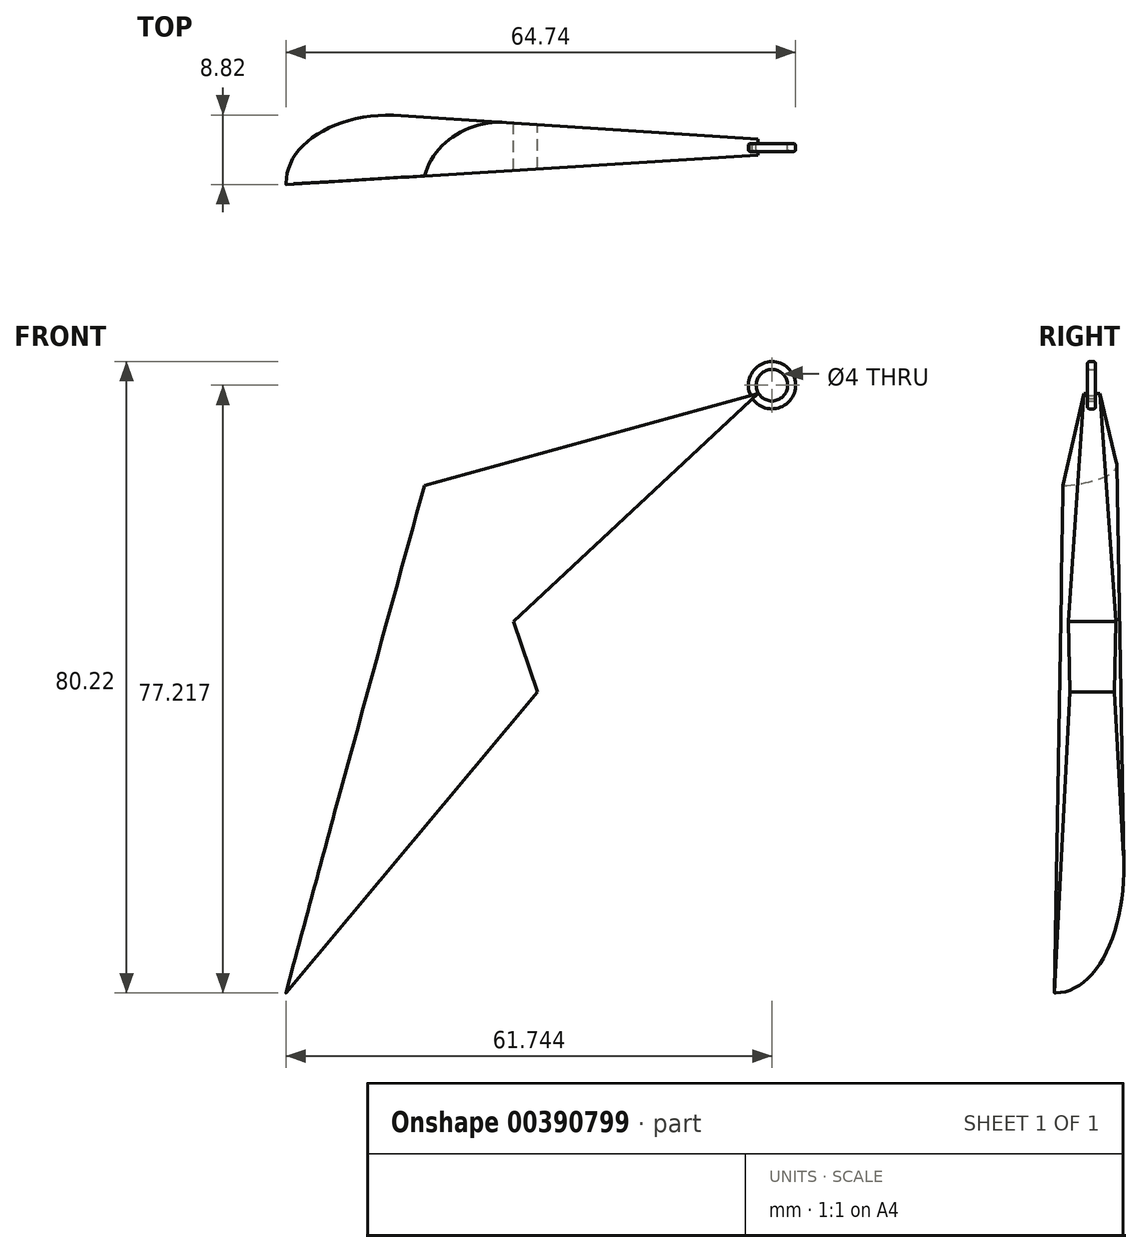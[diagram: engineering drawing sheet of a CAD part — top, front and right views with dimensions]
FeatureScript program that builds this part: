
annotation { "Feature Type Name" : "Feature", "Feature Type Description" : "" }
export const myFeature = defineFeature(function(context is Context, id is Id, definition is map)
    precondition{}
    {
        {
            var Q0;
            Q0=qCreatedBy(makeId("Front.planeOp"),FACE);
            var sketch = newSketch(context, id + "F0", { "sketchPlane" : qUnion([Q0])});
            skLineSegment(sketch, "E0", {"start": v(-11.57, 18.72) * mm, "end": v(-28.9, -45.65) * mm});
            skLineSegment(sketch, "E1", {"start": v(-28.9, -45.65) * mm, "end": v(3.1, -7.37) * mm});
            skLineSegment(sketch, "E2", {"start": v(3.1, -7.37) * mm, "end": v(0, 1.58) * mm});
            skLineSegment(sketch, "E3", {"start": v(0, 1.58) * mm, "end": v(31.1, 30.53) * mm});
            skLineSegment(sketch, "E4", {"start": v(31.1, 30.53) * mm, "end": v(-11.57, 18.72) * mm});
            skSolve(sketch);
        }
        {
            var Q0;
            Q0=makeQuery(id+"F0.imprint","IMPRINT",FACE,{"disambiguationData":[TD([[makeQuery(id+"F0.imprint","IMPRINT",EDGE,{"derivedFrom":sQuery(id+"F0.wireOp",EDGE,"E0")}),1.0]])]});
            extrude(context, id + "F1", {"entities" : qUnion([Q0]), "depth" : 5 * mm, "hasSecondDirection" : true, "secondDirectionOppositeDirection" : true, "secondDirectionDepth" : 5 * mm});
        }
        {
            var Q0;
            Q0=qCreatedBy(makeId("Top.planeOp"),FACE);
            var sketch = newSketch(context, id + "F2", { "sketchPlane" : qUnion([Q0])});
            skLineSegment(sketch, "E5", {"start": v(-39.09, 5.72) * mm, "end": v(-39.09, -5.33) * mm});
            skLineSegment(sketch, "E6", {"start": v(-39.09, -5.33) * mm, "end": v(47.13, 0) * mm});
            skLineSegment(sketch, "E7", {"start": v(47.13, 0) * mm, "end": v(-39.09, 5.72) * mm});
            skLineSegment(sketch, "E8", {"start": v(-48.28, 20.76) * mm, "end": v(52.08, 20.76) * mm});
            skLineSegment(sketch, "E9", {"start": v(52.08, 20.76) * mm, "end": v(52.08, -13.52) * mm});
            skLineSegment(sketch, "E10", {"start": v(52.08, -13.52) * mm, "end": v(-48.28, -13.52) * mm});
            skLineSegment(sketch, "E11", {"start": v(-48.28, -13.52) * mm, "end": v(-48.28, 20.76) * mm});
            skSolve(sketch);
        }
        {
            var Q0;
            Q0=makeQuery(id+"F2.imprint","IMPRINT",FACE,{"disambiguationData":[TD([[makeQuery(id+"F2.imprint","IMPRINT",EDGE,{"derivedFrom":sQuery(id+"F2.wireOp",EDGE,"E5")}),-1.0]])]});
            extrude(context, id + "F3", {"entities" : qUnion([Q0]), "operationType" : NewBodyOperationType.REMOVE, "oppositeDirection" : true, "depth" : 63.9 * mm, "hasSecondDirection" : true, "secondDirectionOppositeDirection" : false, "secondDirectionDepth" : 50 * mm});
        }
        {
            var Q0;
            Q0=makeQuery(id+"F3.boolean.opBoolean","INTERSECT",EDGE,{"derivedFrom":[makeQuery(id+"F1.opExtrude","SWEPT_FACE",FACE,{"disambiguationData":[OSD([sQuery(id+"F0.wireOp",EDGE,"E0")])]}),makeQuery(id+"F3.opExtrude","SWEPT_FACE",FACE,{"disambiguationData":[OSD([sQuery(id+"F2.wireOp",EDGE,"E6")])]})]});
            fillet(context, id + "F4", {"entities" : qUnion([Q0]), "radius" : 0.02 * mm, "tangentPropagation" : true, "allowEdgeOverflow" : false});
        }
        {
            var Q0;
            Q0=makeQuery(id+"F3.boolean.opBoolean","INTERSECT",EDGE,{"derivedFrom":[makeQuery(id+"F1.opExtrude","SWEPT_FACE",FACE,{"disambiguationData":[OSD([sQuery(id+"F0.wireOp",EDGE,"E0")])]}),makeQuery(id+"F3.opExtrude","SWEPT_FACE",FACE,{"disambiguationData":[OSD([sQuery(id+"F2.wireOp",EDGE,"E7")])]})]});
            var Q1;
            {var subQ0=makeQuery(id+"F1.opExtrude","SWEPT_FACE",FACE,{"disambiguationData":[OSD([sQuery(id+"F0.wireOp",EDGE,"E0")])]});Q1=makeQuery(id+"F4.opFillet","BLEND_EDGE",EDGE,{"blendedFrom":[makeQuery(id+"F3.boolean.opBoolean","INTERSECT",EDGE,{"derivedFrom":[subQ0,makeQuery(id+"F3.opExtrude","SWEPT_FACE",FACE,{"disambiguationData":[OSD([sQuery(id+"F2.wireOp",EDGE,"E6")])]})]}),subQ0],"blendedInto":[subQ0]});}
            fillet(context, id + "F5", {"entities" : qUnion([Q0, Q1]), "radius" : 9 * mm, "tangentPropagation" : true, "allowEdgeOverflow" : false});
        }
        {
            var Q0;
            Q0=qCreatedBy(makeId("Front.planeOp"),FACE);
            var sketch = newSketch(context, id + "F6", { "sketchPlane" : qUnion([Q0])});
            skCircle(sketch, "E12", {"center": v(32.84, 31.57) * mm, "radius": 2 * mm});
            skCircle(sketch, "E13.0", {"center": v(32.84, 31.57) * mm, "radius": 3 * mm});
            skSolve(sketch);
        }
        {
            var Q0;
            Q0=makeQuery(id+"F6.imprint","IMPRINT",FACE,{"disambiguationData":[TD([[makeQuery(id+"F6.imprint","IMPRINT",EDGE,{"derivedFrom":sQuery(id+"F6.wireOp",EDGE,"E12")}),-1.0]])]});
            extrude(context, id + "F7", {"entities" : qUnion([Q0]), "operationType" : NewBodyOperationType.ADD, "depth" : .5 * mm, "hasSecondDirection" : true, "secondDirectionOppositeDirection" : true, "secondDirectionDepth" : .5 * mm});
        }
        {
            var Q0;
            Q0=makeQuery(id+"F7.opExtrude","CAP_EDGE",EDGE,{"disambiguationData":[OSD([sQuery(id+"F6.wireOp",EDGE,"E13.0")])],"isStart":true});
            var Q1;
            Q1=makeQuery(id+"F7.opExtrude","CAP_EDGE",EDGE,{"disambiguationData":[OSD([sQuery(id+"F6.wireOp",EDGE,"E12")])],"isStart":false});
            var Q2;
            Q2=makeQuery(id+"F7.opExtrude","CAP_EDGE",EDGE,{"disambiguationData":[OSD([sQuery(id+"F6.wireOp",EDGE,"E12")])],"isStart":true});
            var Q3;
            Q3=makeQuery(id+"F7.opExtrude","CAP_EDGE",EDGE,{"disambiguationData":[OSD([sQuery(id+"F6.wireOp",EDGE,"E13.0")])],"isStart":false});
            fillet(context, id + "F8", {"entities" : qUnion([Q0, Q1, Q2, Q3]), "radius" : .25 * mm, "tangentPropagation" : true, "allowEdgeOverflow" : false});
        }
    });
